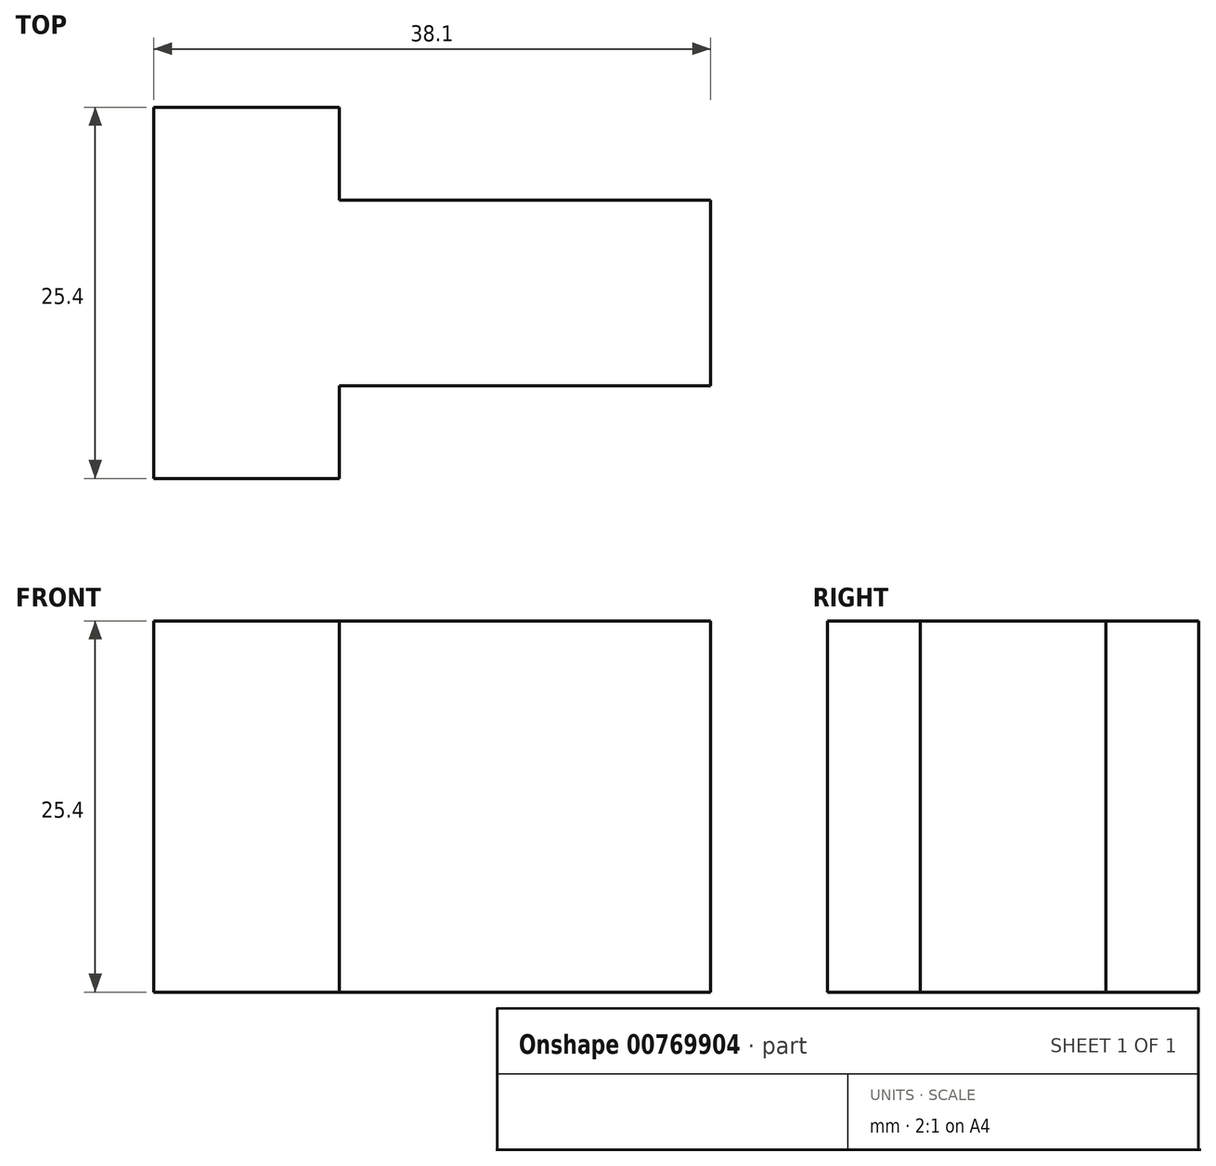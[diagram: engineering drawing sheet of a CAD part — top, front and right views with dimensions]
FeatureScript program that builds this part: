
annotation { "Feature Type Name" : "Feature", "Feature Type Description" : "" }
export const myFeature = defineFeature(function(context is Context, id is Id, definition is map)
    precondition{}
    {
        {
            var Q0;
            Q0=qCreatedBy(makeId("Top.planeOp"),FACE);
            var sketch = newSketch(context, id + "F0", { "sketchPlane" : qUnion([Q0])});
            skLineSegment(sketch, "E0", {"start": v(0, 0) * mm, "end": v(25.4, 0) * mm});
            skLineSegment(sketch, "E1", {"start": v(25.4, 0) * mm, "end": v(25.4, 12.7) * mm});
            skLineSegment(sketch, "E2", {"start": v(25.4, 12.7) * mm, "end": v(0, 12.7) * mm});
            skLineSegment(sketch, "E3", {"start": v(0, 12.7) * mm, "end": v(0, 19.05) * mm});
            skLineSegment(sketch, "E4", {"start": v(0, 19.05) * mm, "end": v(-12.7, 19.05) * mm});
            skLineSegment(sketch, "E5", {"start": v(-12.7, 19.05) * mm, "end": v(-12.7, -6.35) * mm});
            skLineSegment(sketch, "E6", {"start": v(-12.7, -6.35) * mm, "end": v(0, -6.35) * mm});
            skLineSegment(sketch, "E7", {"start": v(0, -6.35) * mm, "end": v(0, 0) * mm});
            skSolve(sketch);
        }
        {
            var Q0;
            Q0 = qSketchRegion(id + "F0", true);
            extrude(context, id + "F1", {"entities" : qUnion([Q0]), "depth" : 25.4 * mm, "offsetDistance" : 25.4 * mm});
        }
    });
